# Revit family: Esserbus transponder FCT set
name_source: partatom
category: Fire Alarm Devices
revit_build: Autodesk Revit 2014 (Build: 20130308_1515(x64)
units: mm (PartAtom-declared; Revit-internal decimal feet)

## types (2) — shared parameters
Apparent Load = 0 VA
IP65 with base attachment = No
Manufacturer = Esser by Honeywell
URL = http://www.esser-systems.com
b1 = 78 mm  [stored 0.255906 ft]
content_date_modified = 16.06.2015
content_version = 1.0
h1 = 141 mm
l1 = 192 mm  [stored 0.629921 ft]
l2 = 236 mm
material = White
material 2 = Black
zero-valued in all types: b2

## per-type parameters (varying)
| type | Model | article number | voltage |
| esserbus transponder FCT set 230 V | esserbus transponder FCT set 230 V | 808600.23 | 230 V |
| esserbus transponder FCT set 12 - 24 V | esserbus transponder FCT set, 12 - 24 V | 808600.24 | 24 V |

note: [stored X ft] marks values corroborated as IEEE doubles in the binary element streams (Revit-internal decimal feet)

## geometry (parser evidence)
native form markers: Sweep x3
no freeform markers — native parametric forms only
